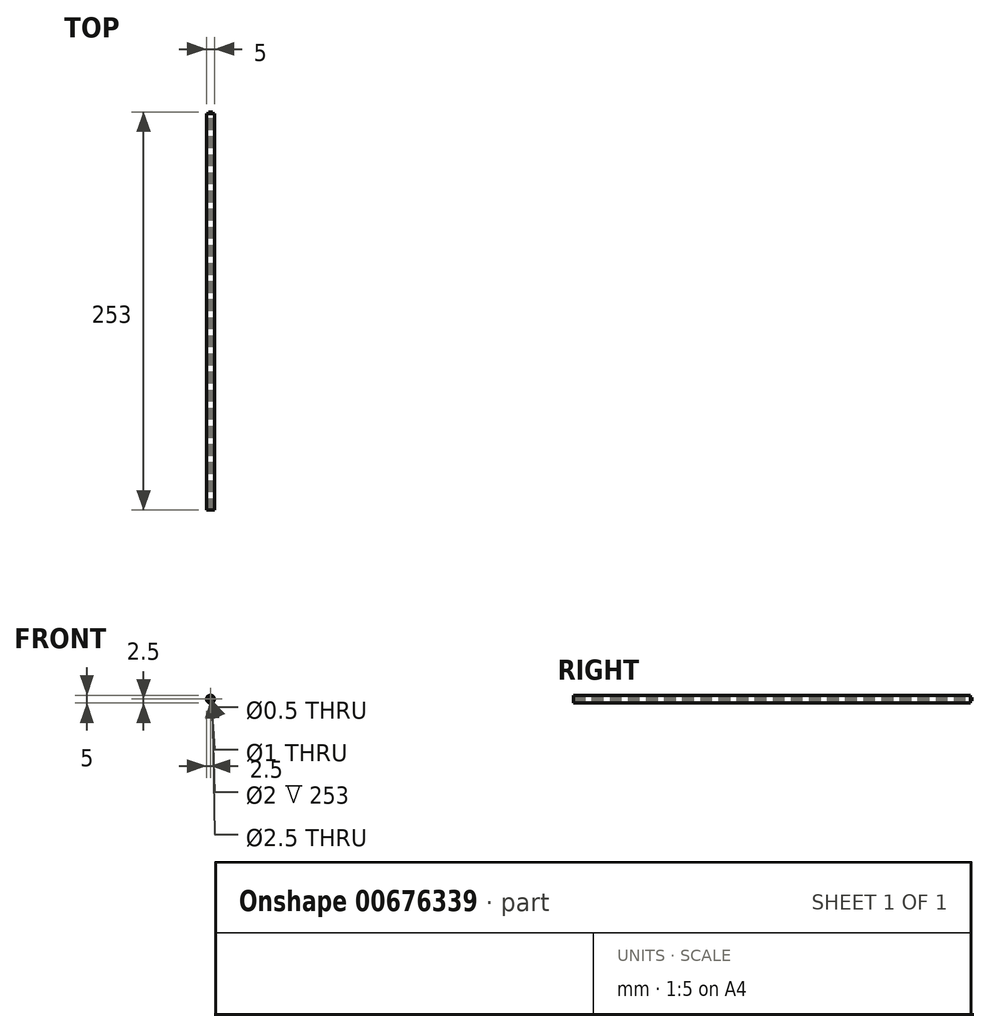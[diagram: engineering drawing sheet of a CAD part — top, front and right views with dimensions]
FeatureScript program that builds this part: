
annotation { "Feature Type Name" : "Feature", "Feature Type Description" : "" }
export const myFeature = defineFeature(function(context is Context, id is Id, definition is map)
    precondition{}
    {
        {
            var Q0;
            Q0=qCreatedBy(makeId("Front.planeOp"),FACE);
            var sketch = newSketch(context, id + "F0", { "sketchPlane" : qUnion([Q0])});
            skCircle(sketch, "E0", {"center": v(0, 0) * mm, "radius": 2.5 * mm});
            skCircle(sketch, "E1", {"center": v(0, 0) * mm, "radius": 1.25 * mm});
            skCircle(sketch, "E2", {"center": v(0, 0) * mm, "radius": 1 * mm});
            skCircle(sketch, "E3", {"center": v(0, 0) * mm, "radius": 0.25 * mm});
            skCircle(sketch, "E4", {"center": v(0, 0) * mm, "radius": 0.5 * mm});
            skSolve(sketch);
        }
        {
            var Q0;
            Q0=makeQuery(id+"F0.imprint","IMPRINT",FACE,{"disambiguationData":[TD([[makeQuery(id+"F0.imprint","IMPRINT",EDGE,{"derivedFrom":sQuery(id+"F0.wireOp",EDGE,"E0")}),1.0]])]});
            var Q1;
            Q1=makeQuery(id+"F0.imprint","IMPRINT",FACE,{"disambiguationData":[TD([[makeQuery(id+"F0.imprint","IMPRINT",EDGE,{"derivedFrom":sQuery(id+"F0.wireOp",EDGE,"E4")}),-1.0]])]});
            var Q2;
            Q2=makeQuery(id+"F0.imprint","IMPRINT",FACE,{"disambiguationData":[TD([[makeQuery(id+"F0.imprint","IMPRINT",EDGE,{"derivedFrom":sQuery(id+"F0.wireOp",EDGE,"E3")}),1.0]])]});
            extrude(context, id + "F1", {"entities" : qUnion([Q0, Q1, Q2]), "depth" : 250 * mm, "offsetDistance" : 25 * mm, "hasSecondDirection" : true, "secondDirectionOppositeDirection" : true, "secondDirectionDepth" : 2 * mm});
        }
        {
            var Q0;
            Q0=makeQuery(id+"F0.imprint","IMPRINT",FACE,{"disambiguationData":[TD([[makeQuery(id+"F0.imprint","IMPRINT",EDGE,{"derivedFrom":sQuery(id+"F0.wireOp",EDGE,"E1")}),1.0]])]});
            var Q1;
            Q1=makeQuery(id+"F0.imprint","IMPRINT",FACE,{"disambiguationData":[TD([[makeQuery(id+"F0.imprint","IMPRINT",EDGE,{"derivedFrom":sQuery(id+"F0.wireOp",EDGE,"E3")}),-1.0]])]});
            extrude(context, id + "F2", {"entities" : qUnion([Q0, Q1]), "depth" : 250 * mm, "offsetDistance" : 25 * mm, "hasSecondDirection" : true, "secondDirectionOppositeDirection" : true, "secondDirectionDepth" : 3 * mm});
        }
    });
